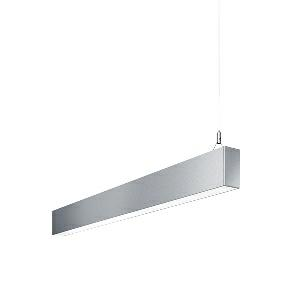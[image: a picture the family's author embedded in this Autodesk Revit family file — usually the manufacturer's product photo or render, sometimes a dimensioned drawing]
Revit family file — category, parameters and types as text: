
# Revit family: dotoo_line_-_dlp_2000_840_d_end_00805828_6f55
name_source: partatom
category: Lighting Fixtures
units: mm (PartAtom-declared; Revit-internal decimal feet)

## family parameters
Cut with Voids When Loaded = No
Host = Face
Light Source = No
Part Type = Normal
Room Calculation Point = No
Round Connector Dimension = Use Diameter
Shared = No

## types (1)
- DOTOO.line - DLP 2000/840/D END (1 x LED, 1700 lm, 4000K)
    Apparent Load = 16 VA
    Approval mark = CE
    CIE Flux Codes = 67 91 98 100 100
    Color Rendering = 80-89
    Color Temperature = 4000K
    Control Gear = Electronic ballast
    Default Elevation = 1800 mm
    Description = DLP 2000/840/D|Suspended luminaire|light source: LED|connected load: 220-240 V, 50/60 Hz|Power consumption: approx. 16 W|standby: approx. 0,15|luminous flux: 1700 lm|luminous efficacy: 106 lm/W|light distribution: Direct|direct ratio: approx. 100 %|colour temperature: Cold white, ca. 4000 K|color rendering index (CRI): >= 80|chromaticity tolerance:  3 SDCM|System of protection: IP 40|technology: Continuously dimmable|luminaire body|material: Sectional aluminium|colour: Silver|lamp cover: Acrylic (PMMA), Clear|mains lead: 1,0 m With free stranded wires|Fastening: Steel cable 0.3 - 0.7 m|glare control: Prism aperture|luminance(L65): <= 3000 cd/m|unified glare rating(4H 8H): <=  19|special features: DALI Load 1x, TouchDIM - dimming via standard switch, Through-wired, up to 18 m on one mains connection, Flicker-free, Suitable as emergency lighting, Mechanical and electrical connection of the individual modules without tools|
    Frequency = 50 Hz
    Height = 110 mm
    Lamp = 1 x LED
    Lamp Light Flux = 1700 lm
    Lamp count = 1
    Length = 1408 mm
    Luminous efficacy = 106 lm/W
    Manufacturer = Waldmann
    ModVariant = No
    Model = 00805828
    Mounting Place = Ceiling
    Mounting Type = Pendant
    Number of Poles = 1
    OnlyDefault = Yes
    Power Factor = 1
    Product Name = DOTOO.line - DLP 2000/840/D END
    Product group = Suspended luminaire
    ProductGroupID = 9
    Protection Class = Protection class I
    Protection Degree = IP 40
    RLX_Detail_Level = 1
    RLX_Emergency_Light_Flux = 0 lm
    RLX_Emergency_Type = 0
    RLX_Emergency_Type_DB = No
    RlxData = <blob elided: 20825 chars, md5=4dd3c1e0>
    Socket = socket
    Standby Power = 0 W
    System Light Flux = 1700 lm
    System Power = 16 W
    Type Comments = Product without accessories
    Type Image = 113312000-00692600.jpg
    URL = http://relux.com
    VarID = ---
    Voltage = 230 V
    Voltage Range = 220-240 V
    Weight = 0.00 kg
    Width = 60 mm  [stored 0.19685 ft]

note: [stored X ft] marks values corroborated as IEEE doubles in the binary element streams (Revit-internal decimal feet)

## geometry (parser evidence)
native form markers: Blend x4, Sweep x12
no freeform markers — native parametric forms only
